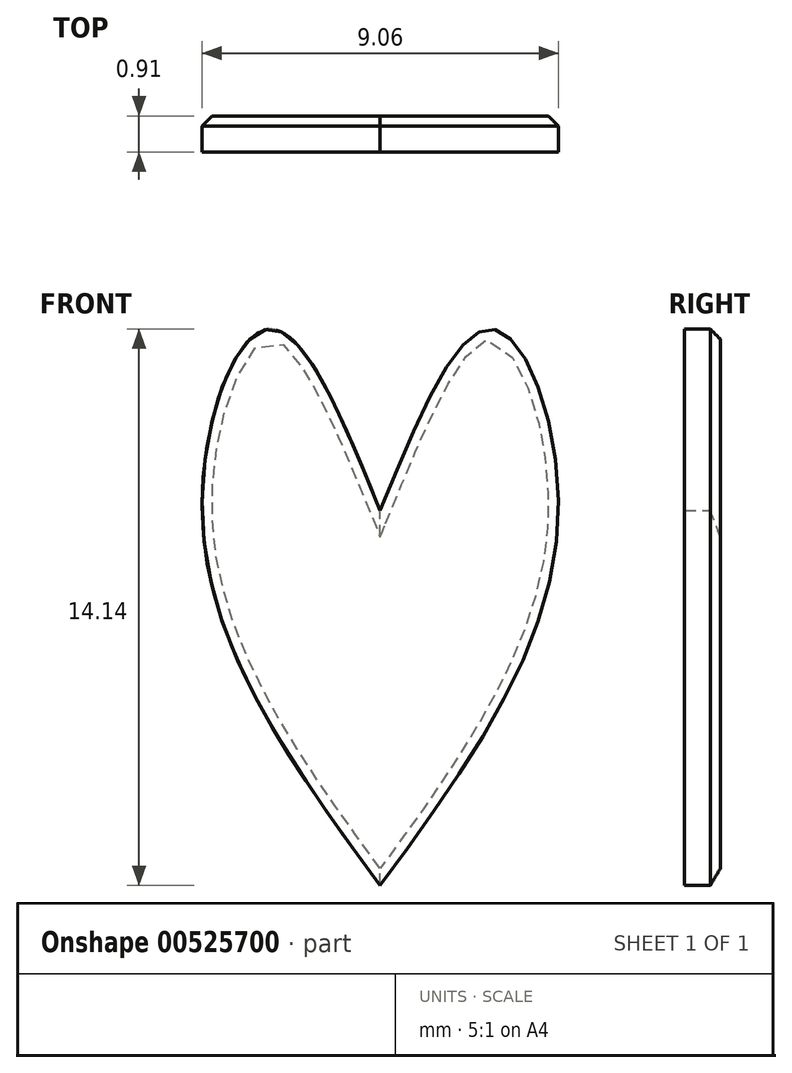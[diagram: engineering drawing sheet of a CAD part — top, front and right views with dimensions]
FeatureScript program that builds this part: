
annotation { "Feature Type Name" : "Feature", "Feature Type Description" : "" }
export const myFeature = defineFeature(function(context is Context, id is Id, definition is map)
    precondition{}
    {
        {
            var Q0;
            Q0=qCreatedBy(makeId("Front.planeOp"),FACE);
            var sketch = newSketch(context, id + "F0", { "sketchPlane" : qUnion([Q0])});
            skFitSpline(sketch, "E0", {"points": [v(0, 1.51) * mm, v(4.51, 10.68) * mm, v(2.86, 15.64) * mm, v(0, 11.04) * mm], "startDerivative": vector(15.85, 21.6) * mm, "endDerivative": vector(-9.71, -23.76) * mm});
            skFitSpline(sketch, "E1.MirrorCS", {"points": [v(0, 1.51) * mm, v(-4.51, 10.68) * mm, v(-2.86, 15.64) * mm, v(0, 11.04) * mm], "startDerivative": vector(-15.85, 21.6) * mm, "endDerivative": vector(9.71, -23.76) * mm});
            skSolve(sketch);
        }
        {
            var Q0;
            Q0=makeQuery(id+"F0.imprint","IMPRINT",FACE,{"disambiguationData":[TD([[makeQuery(id+"F0.imprint","IMPRINT",EDGE,{"derivedFrom":sQuery(id+"F0.wireOp",EDGE,"E0")}),1.0]])]});
            extrude(context, id + "F1", {"entities" : qUnion([Q0]), "depth" : 0.91 * mm, "offsetDistance" : 25.4 * mm});
        }
        {
            var Q0;
            Q0=makeQuery(id+"F1.opExtrude","CAP_EDGE",EDGE,{"disambiguationData":[OSD([sQuery(id+"F0.wireOp",EDGE,"E0")])],"isStart":true});
            chamfer(context, id + "F2", {"entities" : qUnion([Q0]), "width" : 0.25 * mm, "tangentPropagation" : true});
        }
        {
            var Q0;
            Q0=makeQuery(id+"F1.opExtrude","CAP_EDGE",EDGE,{"disambiguationData":[OSD([sQuery(id+"F0.wireOp",EDGE,"E1.MirrorCS")])],"isStart":true});
            chamfer(context, id + "F3", {"entities" : qUnion([Q0]), "width" : 0.25 * mm, "tangentPropagation" : true});
        }
    });
